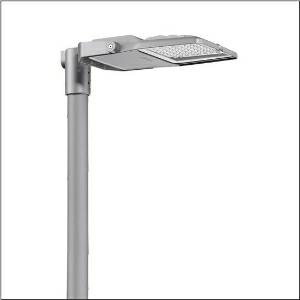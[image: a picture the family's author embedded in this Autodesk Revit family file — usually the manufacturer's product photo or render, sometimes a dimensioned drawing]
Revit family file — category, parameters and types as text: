
# Revit family: floodlight_fl_21_mini___pl52_5xa7775c2d3a_b3eb
name_source: partatom
category: Lighting Fixtures
units: mm (PartAtom-declared; Revit-internal decimal feet)

## family parameters
Cut with Voids When Loaded = No
Host = Face
Light Source = No
Part Type = Normal
Room Calculation Point = No
Round Connector Dimension = Use Diameter
Shared = No

## types (1)
- --- (1 x LED, 12190 lm, 89 W, 3000K)
    Apparent Load = 89 VA
    CIE Flux Codes = 26 60 98 100 100
    Color Rendering = 70
    Color Temperature = 3000K
    Default Elevation = 1800 mm
    Description = Floodlight FL 21 mini, floodlight, primary light control with lens, of PMMA, primary optical cover: protective disc, of toughened safety glass, transparent, light distribution: PL52, light emission: direct distribution, installation type: surface-mounted, LED, High Power LED, rated luminous flux: 12.190lm, luminous efficacy: 137lm/W, light colour: 730, colour temperature: 3000K, control gear: ECG Smart Interface, control: flexible luminous flux parameterisation, time-dependent luminous flux control, constant luminous flux control, overheat protection, presetting dimming logarithmic, with terminal, 6-pole, mains connection: 220..240V, AC, 50/60Hz, start of lifetime: 89W, end of lifetime: 94W, reduction: 43W, luminaire housing, of diecast aluminium, powder-coated, Siteco® metallic grey (DB 702S), corrosivity category C5 according to DIN EN ISO 12944, mast bracket, of steel, galvanised, powder-coated, Siteco® metallic grey (DB 702S), protection rating (complete): IP66, insulation class (complete): insulation class II (safety insulation), certification: CE, ENEC, VDE, protection symbol: D, impact resistance: IK08, permissible operating ambient temperature: -40..+40°C, permissible operating ambient temperature for outdoor applications: -40..+50°C, standard: DIN EN 12944, packaging unit: 1 piece

Light Distribution: PL52
    Height = 70 mm
    Lamp = 1 x LED
    Lamp Light Flux = 12190 lm
    Lamp Power = 89 W
    Lamp count = 1
    Length = 485 mm
    Luminous efficacy = 137 lm/W
    Manufacturer = Siteco
    ModVariant = No
    Model = 5XA7775C2D3A
    Number of Poles = 1
    OnlyDefault = Yes
    Power Factor = 1
    Product Name = Floodlight FL 21 mini | PL52
    Product group = floodlight | pylon top
    ProductGroupID = 6101
    Protection Class = Protection class II
    Protection Degree = IP 66
    RLX_Detail_Level = 1
    RlxData = <blob elided: 100913 chars, md5=8495c175>
    Socket = socket
    Standby Power = 0 W
    System Light Flux = 12190 lm
    System Power = 89 W
    Type Comments = factory setting: luminous flux: 100 % | dim-lin: 254 | 456 mA
    Type Image = l_1007125.jpg
    URL = http://relux.com
    VarID = @adj_074509
    Voltage = 0 V
    Weight = 0.00 kg
    Width = 337 mm

## geometry (parser evidence)
native form markers: Blend x4, Sweep x12
no freeform markers — native parametric forms only
